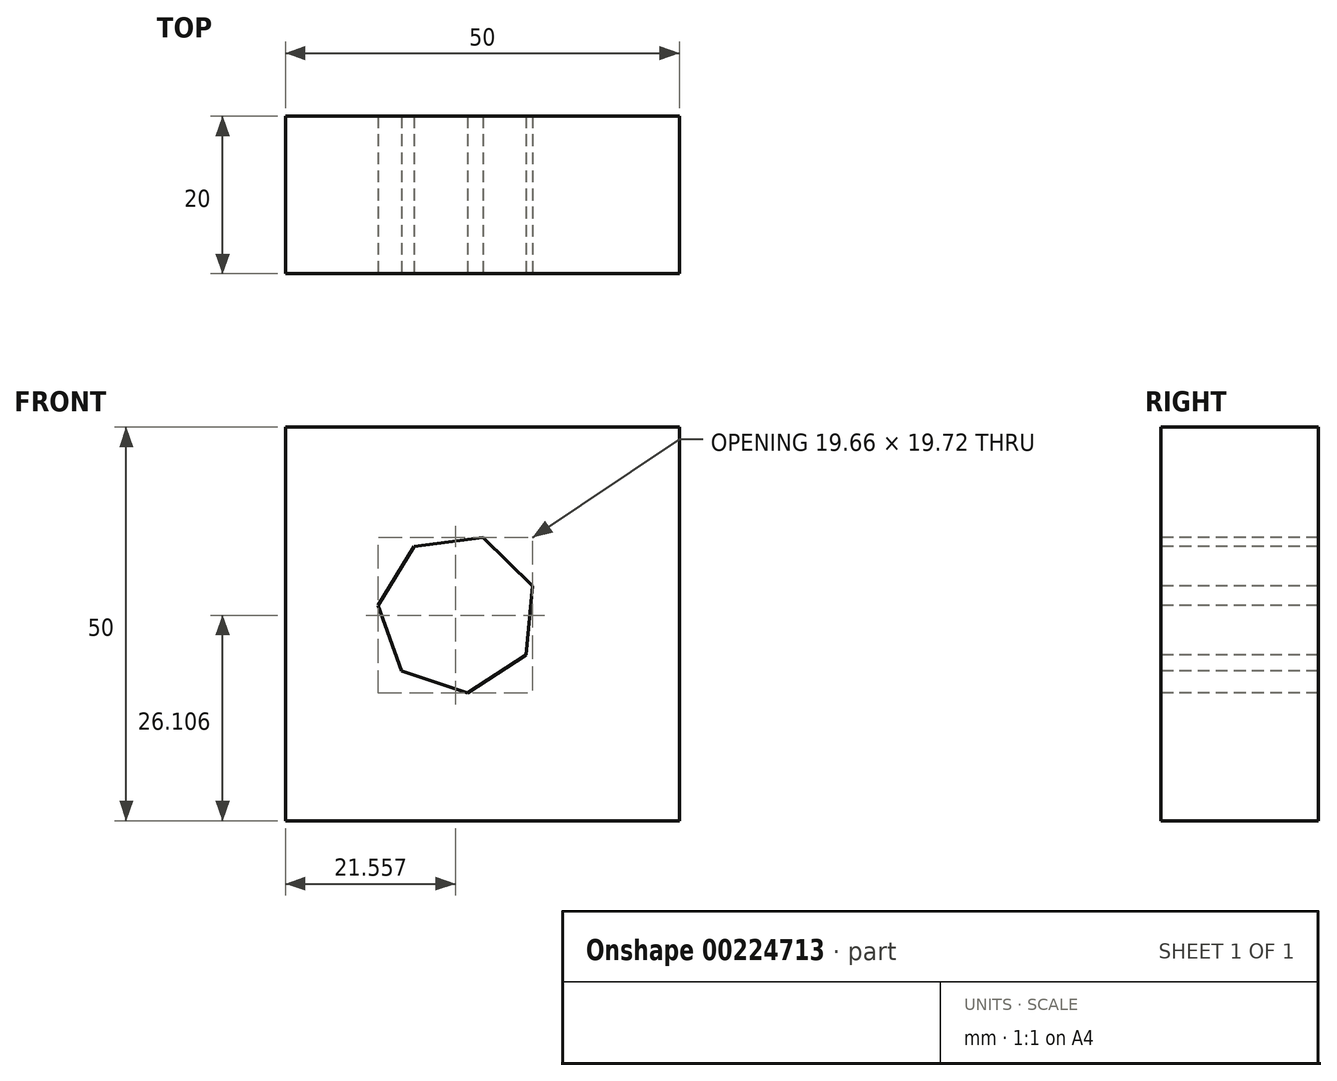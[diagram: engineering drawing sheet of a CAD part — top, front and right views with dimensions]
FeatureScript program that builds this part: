
annotation { "Feature Type Name" : "Feature", "Feature Type Description" : "" }
export const myFeature = defineFeature(function(context is Context, id is Id, definition is map)
    precondition{}
    {
        {
            var Q0;
            Q0=qCreatedBy(makeId("Front.planeOp"),FACE);
            var sketch = newSketch(context, id + "F0", { "sketchPlane" : qUnion([Q0])});
            skLineSegment(sketch, "E0", {"start": v(0, 0) * mm, "end": v(0, 50) * mm});
            skLineSegment(sketch, "E1", {"start": v(0, 50) * mm, "end": v(50, 50) * mm});
            skLineSegment(sketch, "E2", {"start": v(50, 50) * mm, "end": v(50, 0) * mm});
            skLineSegment(sketch, "E3", {"start": v(50, 0) * mm, "end": v(0, 0) * mm});
            skSolve(sketch);
        }
        {
            var Q0;
            Q0=makeQuery(id+"F0.imprint","IMPRINT",FACE,{"disambiguationData":[TD([[makeQuery(id+"F0.imprint","IMPRINT",EDGE,{"derivedFrom":sQuery(id+"F0.wireOp",EDGE,"E0")}),-1.0]])]});
            extrude(context, id + "F1", {"entities" : qUnion([Q0]), "depth" : 20 * mm});
        }
        {
            var Q0;
            Q0=makeQuery(id+"F1.opExtrude","CAP_FACE",FACE,{"disambiguationData":[OSD([sQuery(id+"F0.wireOp",EDGE,"E0"),sQuery(id+"F0.wireOp",EDGE,"E1"),sQuery(id+"F0.wireOp",EDGE,"E2"),sQuery(id+"F0.wireOp",EDGE,"E3")])],"isStart":false});
            var sketch = newSketch(context, id + "F2", { "sketchPlane" : qUnion([Q0])});
            skCircle(sketch, "E4.cCircle", {"center": v(21.84, 26.33) * mm, "radius": 10.16 * mm, "construction": true});
            skLineSegment(sketch, "E4.0", {"start": v(16.32, 34.86) * mm, "end": v(25.07, 35.97) * mm});
            skLineSegment(sketch, "E4.1", {"start": v(25.07, 35.97) * mm, "end": v(31.39, 29.81) * mm});
            skLineSegment(sketch, "E4.2", {"start": v(31.39, 29.81) * mm, "end": v(30.52, 21.04) * mm});
            skLineSegment(sketch, "E4.3", {"start": v(30.52, 21.04) * mm, "end": v(23.12, 16.25) * mm});
            skLineSegment(sketch, "E4.4", {"start": v(23.12, 16.25) * mm, "end": v(14.75, 19.05) * mm});
            skLineSegment(sketch, "E4.5", {"start": v(14.75, 19.05) * mm, "end": v(11.73, 27.33) * mm});
            skLineSegment(sketch, "E4.6", {"start": v(11.73, 27.33) * mm, "end": v(16.32, 34.86) * mm});
            skSolve(sketch);
        }
        {
            var Q0;
            Q0=makeQuery(id+"F2.imprint","IMPRINT",FACE,{"disambiguationData":[TD([[makeQuery(id+"F2.imprint","IMPRINT",EDGE,{"derivedFrom":sQuery(id+"F2.wireOp",EDGE,"E4.0")}),-1.0]])]});
            extrude(context, id + "F3", {"entities" : qUnion([Q0]), "operationType" : NewBodyOperationType.REMOVE, "oppositeDirection" : true, "depth" : 44.2 * mm});
        }
    });
